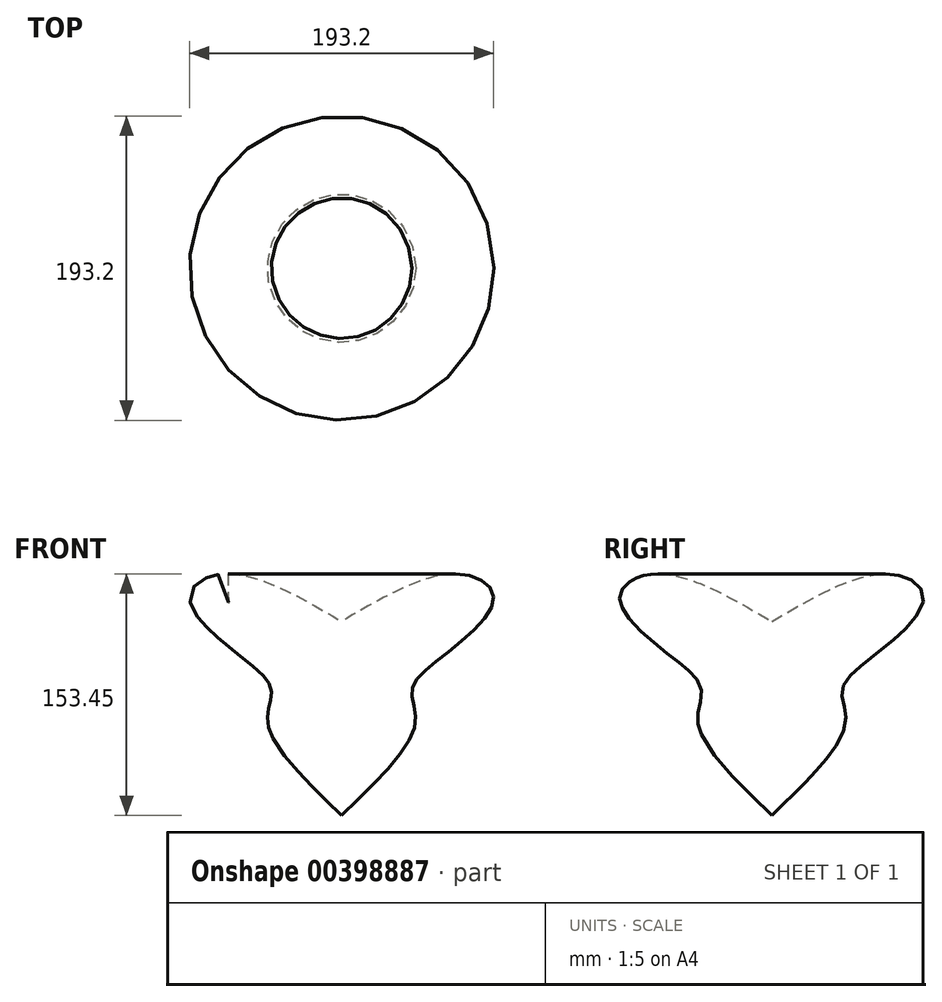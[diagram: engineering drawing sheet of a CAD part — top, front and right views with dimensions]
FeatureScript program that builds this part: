
annotation { "Feature Type Name" : "Feature", "Feature Type Description" : "" }
export const myFeature = defineFeature(function(context is Context, id is Id, definition is map)
    precondition{}
    {
        {
            var Q0;
            Q0=qCreatedBy(makeId("Front.planeOp"),FACE);
            var sketch = newSketch(context, id + "F0", { "sketchPlane" : qUnion([Q0])});
            skLineSegment(sketch, "E0", {"start": v(-66.27, 69.35) * mm, "end": v(-66.27, -53.88) * mm});
            skFitSpline(sketch, "E1", {"points": [v(-66.27, -53.88) * mm, v(-19.39, 4.63) * mm, v(-21.5, 26.22) * mm, v(2.47, 50.77) * mm, v(30.31, 84.89) * mm, v(7.75, 99.53) * mm, v(-66.27, 69.35) * mm], "startDerivative": vector(308.47, 296.07) * mm, "endDerivative": vector(-357, -208.55) * mm});
            skSolve(sketch);
        }
        {
            var Q0;
            Q0=makeQuery(id+"F0.imprint","IMPRINT",FACE,{"disambiguationData":[TD([[makeQuery(id+"F0.imprint","IMPRINT",EDGE,{"derivedFrom":sQuery(id+"F0.wireOp",EDGE,"E0")}),1.0]])]});
            var Q1;
            Q1=sQuery(id+"F0.wireOp",EDGE,"E0");
            revolve(context, id + "F1", {"entities" : qUnion([Q0]), "axis" : qUnion([Q1]), "revolveType" : RevolveType.FULL});
        }
    });
